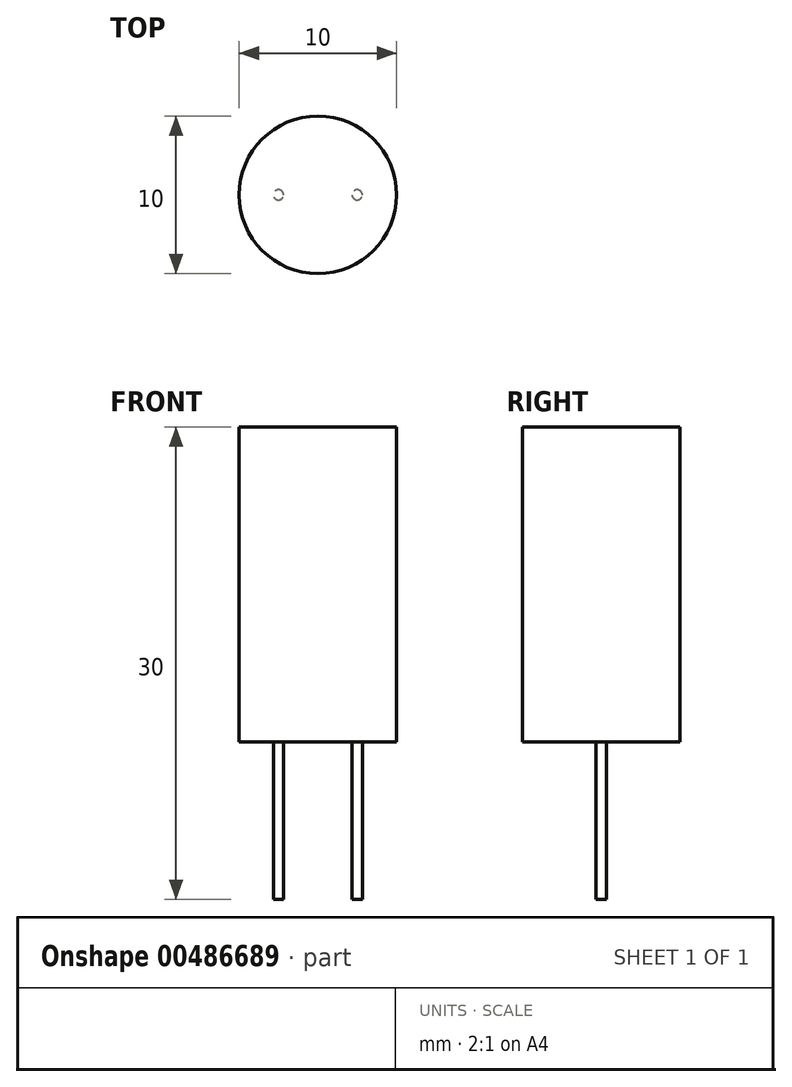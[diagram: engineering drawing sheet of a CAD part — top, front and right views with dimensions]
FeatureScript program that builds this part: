
annotation { "Feature Type Name" : "Feature", "Feature Type Description" : "" }
export const myFeature = defineFeature(function(context is Context, id is Id, definition is map)
    precondition{}
    {
        {
            var Q0;
            Q0=qCreatedBy(makeId("Top.planeOp"),FACE);
            var sketch = newSketch(context, id + "F0", { "sketchPlane" : qUnion([Q0])});
            skCircle(sketch, "E0", {"center": v(0, 0) * mm, "radius": 5 * mm});
            skSolve(sketch);
        }
        {
            var Q0;
            Q0=qSketchRegion(id+"F0",true);
            extrude(context, id + "F1", {"entities" : qUnion([Q0]), "depth" : 20 * mm});
        }
        {
            var Q0;
            Q0=makeQuery(id+"F1.opExtrude","CAP_FACE",FACE,{"disambiguationData":[OSD([sQuery(id+"F0.wireOp",EDGE,"E0")])],"isStart":true});
            var sketch = newSketch(context, id + "F2", { "sketchPlane" : qUnion([Q0])});
            skCircle(sketch, "E1", {"center": v(-2.5, 0) * mm, "radius": 0.33 * mm});
            skCircle(sketch, "E2", {"center": v(2.5, 0) * mm, "radius": 0.33 * mm});
            skSolve(sketch);
        }
        {
            var Q0;
            Q0=qSketchRegion(id+"F2",true);
            extrude(context, id + "F3", {"entities" : qUnion([Q0]), "operationType" : NewBodyOperationType.ADD, "depth" : 10 * mm});
        }
    });
